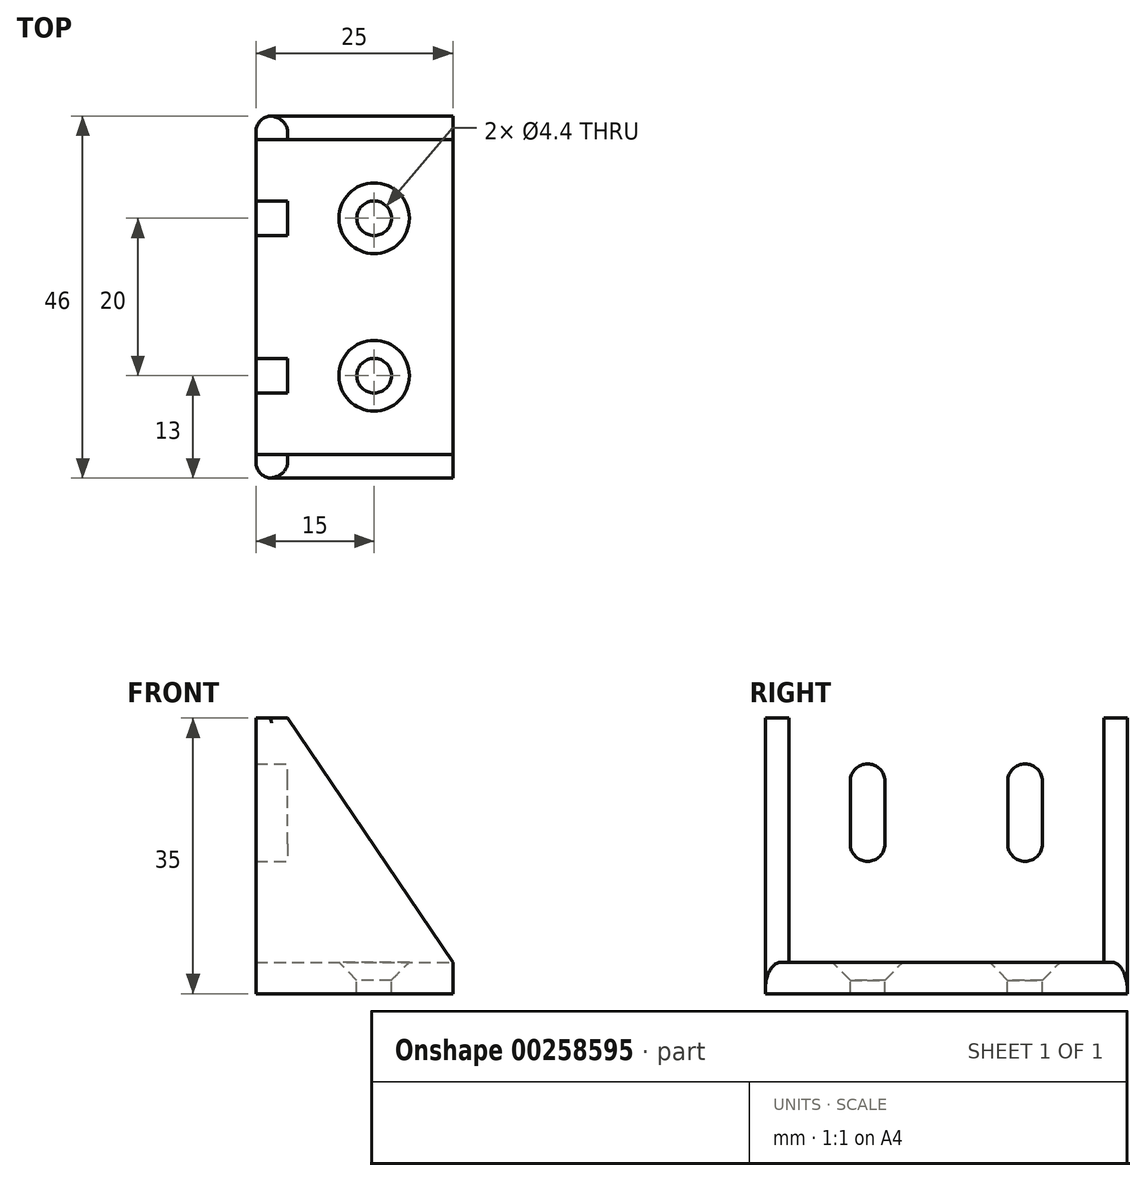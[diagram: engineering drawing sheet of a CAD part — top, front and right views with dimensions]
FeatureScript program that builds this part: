
annotation { "Feature Type Name" : "Feature", "Feature Type Description" : "" }
export const myFeature = defineFeature(function(context is Context, id is Id, definition is map)
    precondition{}
    {
        {
            var Q0;
            Q0=qCreatedBy(makeId("Front.planeOp"),FACE);
            var sketch = newSketch(context, id + "F0", { "sketchPlane" : qUnion([Q0])});
            skLineSegment(sketch, "E0.bottom", {"start": v(-12.5, -17.5) * mm, "end": v(12.5, -17.5) * mm});
            skLineSegment(sketch, "E0.top", {"start": v(-12.5, 17.5) * mm, "end": v(-8.5, 17.5) * mm});
            skLineSegment(sketch, "E0.left", {"start": v(-12.5, -17.5) * mm, "end": v(-12.5, 17.5) * mm});
            skLineSegment(sketch, "E0.right", {"start": v(12.5, -17.5) * mm, "end": v(12.5, -13.5) * mm});
            skPoint(sketch, "E0.middle", {"position": v(0, 0) * mm});
            skLineSegment(sketch, "E1.0", {"start": v(-8.5, -13.5) * mm, "end": v(-8.5, 17.5) * mm});
            skLineSegment(sketch, "E1.1", {"start": v(-8.5, -13.5) * mm, "end": v(12.5, -13.5) * mm});
            skSolve(sketch);
        }
        {
            var Q0;
            Q0 = qSketchRegion(id + "F0", true);
            extrude(context, id + "F1", {"entities" : qUnion([Q0]), "depth" : 40 * mm});
        }
        {
            var Q0;
            Q0=makeQuery(id+"F1.opExtrude","SWEPT_FACE",FACE,{"disambiguationData":[OSD([sQuery(id+"F0.wireOp",EDGE,"E1.0")])]});
            var sketch = newSketch(context, id + "F2", { "sketchPlane" : qUnion([Q0])});
            skPoint(sketch, "E2", {"position": v(-30, 9.5) * mm});
            skPoint(sketch, "E3.1.0.0", {"position": v(-10, 5) * mm});
            skLineSegment(sketch, "E4", {"start": v(-20, 17.5) * mm, "end": v(-20, -13.5) * mm, "construction": true});
            skArc(sketch, "E5", {"start": v(-7.8, 9.5) * mm, "mid": v(-10, 11.7) * mm, "end": v(-12.2, 9.5) * mm});
            skArc(sketch, "E6.MirrorC", {"start": v(-7.8, 1.5) * mm, "mid": v(-10, -0.7) * mm, "end": v(-12.2, 1.5) * mm});
            skArc(sketch, "E7.MirrorC", {"start": v(-32.2, 9.5) * mm, "mid": v(-30, 11.7) * mm, "end": v(-27.8, 9.5) * mm});
            skArc(sketch, "E8.MirrorC", {"start": v(-32.2, 1.5) * mm, "mid": v(-30, -0.7) * mm, "end": v(-27.8, 1.5) * mm});
            skLineSegment(sketch, "E9", {"start": v(-7.8, 1.5) * mm, "end": v(-7.8, 9.5) * mm});
            skLineSegment(sketch, "E10", {"start": v(-12.2, 1.5) * mm, "end": v(-12.2, 9.5) * mm});
            skLineSegment(sketch, "E11.MirrorCS", {"start": v(-27.8, 1.5) * mm, "end": v(-27.8, 9.5) * mm});
            skLineSegment(sketch, "E12.MirrorCS", {"start": v(-32.2, 1.5) * mm, "end": v(-32.2, 9.5) * mm});
            skSolve(sketch);
        }
        {
            var Q0;
            Q0=makeQuery(id+"F2.imprint","IMPRINT",FACE,{"disambiguationData":[TD([[makeQuery(id+"F2.imprint","IMPRINT",EDGE,{"derivedFrom":sQuery(id+"F2.wireOp",EDGE,"E7.MirrorC")}),-1.0]])]});
            var Q1;
            Q1=makeQuery(id+"F2.imprint","IMPRINT",FACE,{"disambiguationData":[TD([[makeQuery(id+"F2.imprint","IMPRINT",EDGE,{"derivedFrom":sQuery(id+"F2.wireOp",EDGE,"E5")}),1.0]])]});
            extrude(context, id + "F3", {"entities" : qUnion([Q0, Q1]), "operationType" : NewBodyOperationType.REMOVE, "endBound" : BoundingType.UP_TO_NEXT, "oppositeDirection" : true, "depth" : 25 * mm});
        }
        {
            var Q0;
            Q0=makeQuery(id+"F1.opExtrude","SWEPT_FACE",FACE,{"disambiguationData":[OSD([sQuery(id+"F0.wireOp",EDGE,"E1.1")])]});
            var sketch = newSketch(context, id + "F4", { "sketchPlane" : qUnion([Q0])});
            skPoint(sketch, "E13", {"position": v(2.5, -30) * mm});
            skLineSegment(sketch, "E14", {"start": v(-8.5, -20) * mm, "end": v(12.5, -20) * mm, "construction": true});
            skPoint(sketch, "E15.MirrorP", {"position": v(2.5, -10) * mm});
            skSolve(sketch);
        }
        {
            var Q0;
            Q0=sQuery(id+"F4.wireOp",VERTEX,"E13");
            var Q1;
            Q1=sQuery(id+"F4.wireOp",VERTEX,"E15.MirrorP");
            var Q2;
            Q2=makeQuery(id+"F1.opExtrude","SWEPT_BODY",BODY,{"disambiguationData":[OSD([sQuery(id+"F0.wireOp",EDGE,"E0.bottom"),sQuery(id+"F0.wireOp",EDGE,"E0.top"),sQuery(id+"F0.wireOp",EDGE,"E0.left"),sQuery(id+"F0.wireOp",EDGE,"E0.right"),sQuery(id+"F0.wireOp",EDGE,"E1.0"),sQuery(id+"F0.wireOp",EDGE,"E1.1")])]});
            hole(context, id + "F5", {"style" : HoleStyle.C_SINK, "endStyle" : HoleEndStyle.THROUGH, "standardTappedOrClearance" : lookupTablePath({ "standard" : "ISO", "fit" : "Normal", "size" : "M4", "type" : "Clearance" }), "standardBlindInLast" : lookupTablePath({ "fit" : "Standard", "standard" : "ISO", "size" : "M4", "type" : "Clearance" }), "holeDiameter" : 4.4 * mm, "cSinkDiameter" : 8.96 * mm, "cSinkAngle" : 90 * degree, "tappedDepth" : 12 * mm, "tapClearance" : 3, "locations" : qUnion([Q0, Q1]), "scope" : qUnion([Q2])});
        }
        {
            var Q0;
            Q0=makeQuery(id+"F1.opExtrude","CAP_FACE",FACE,{"disambiguationData":[OSD([sQuery(id+"F0.wireOp",EDGE,"E0.bottom"),sQuery(id+"F0.wireOp",EDGE,"E0.top"),sQuery(id+"F0.wireOp",EDGE,"E0.left"),sQuery(id+"F0.wireOp",EDGE,"E0.right"),sQuery(id+"F0.wireOp",EDGE,"E1.0"),sQuery(id+"F0.wireOp",EDGE,"E1.1")])],"isStart":false});
            var sketch = newSketch(context, id + "F6", { "sketchPlane" : qUnion([Q0])});
            skLineSegment(sketch, "E16", {"start": v(-8.5, 17.5) * mm, "end": v(12.5, -13.5) * mm});
            skLineSegment(sketch, "E17", {"start": v(12.5, -13.5) * mm, "end": v(12.5, -17.5) * mm});
            skLineSegment(sketch, "E18", {"start": v(12.5, -17.5) * mm, "end": v(-12.5, -17.5) * mm});
            skLineSegment(sketch, "E19", {"start": v(-12.5, -17.5) * mm, "end": v(-12.5, 17.5) * mm});
            skLineSegment(sketch, "E20", {"start": v(-12.5, 17.5) * mm, "end": v(-8.5, 17.5) * mm});
            skSolve(sketch);
        }
        {
            var Q0;
            Q0 = qSketchRegion(id + "F6", true);
            extrude(context, id + "F7", {"entities" : qUnion([Q0]), "operationType" : NewBodyOperationType.ADD, "depth" : 3 * mm});
        }
        {
            var Q0;
            Q0=makeQuery(id+"F1.opExtrude","CAP_FACE",FACE,{"disambiguationData":[OSD([sQuery(id+"F0.wireOp",EDGE,"E0.bottom"),sQuery(id+"F0.wireOp",EDGE,"E0.top"),sQuery(id+"F0.wireOp",EDGE,"E0.left"),sQuery(id+"F0.wireOp",EDGE,"E0.right"),sQuery(id+"F0.wireOp",EDGE,"E1.0"),sQuery(id+"F0.wireOp",EDGE,"E1.1")])],"isStart":true});
            cPlane(context, id + "F8", {"entities" : qUnion([Q0]), "cplaneType" : CPlaneType.OFFSET, "offset" : 20 * mm, "oppositeDirection" : true, "width" : 150 * mm, "height" : 150 * mm});
        }
        {
            var Q0;
            Q0=makeQuery(id+"F1.opExtrude","SWEPT_BODY",BODY,{"disambiguationData":[OSD([sQuery(id+"F0.wireOp",EDGE,"E0.bottom"),sQuery(id+"F0.wireOp",EDGE,"E0.top"),sQuery(id+"F0.wireOp",EDGE,"E0.left"),sQuery(id+"F0.wireOp",EDGE,"E0.right"),sQuery(id+"F0.wireOp",EDGE,"E1.0"),sQuery(id+"F0.wireOp",EDGE,"E1.1")])]});
            var Q1;
            Q1=qCreatedBy(id+"F8.planeOp",FACE);
            mirror(context, id + "F9", {"operationType" : NewBodyOperationType.ADD, "entities" : qUnion([Q0]), "mirrorPlane" : qUnion([Q1])});
        }
        {
            var Q0;
            Q0=makeQuery(id+"F1.opExtrude","CAP_EDGE",EDGE,{"disambiguationData":[OSD([sQuery(id+"F0.wireOp",EDGE,"E1.0")])],"isStart":false});
            var Q1;
            Q1=makeQuery(id+"F1.opExtrude","CAP_EDGE",EDGE,{"disambiguationData":[OSD([sQuery(id+"F0.wireOp",EDGE,"E1.1")])],"isStart":false});
            var Q2;
            Q2=makeQuery(id+"F1.opExtrude","SWEPT_EDGE",EDGE,{"disambiguationData":[OSD([sQuery(id+"F0.wireOp",EDGE,"E1.0"),sQuery(id+"F0.wireOp",EDGE,"E1.1")])]});
            var Q3;
            {var subQ0=sQuery(id+"F0.wireOp",EDGE,"E1.1");Q3=makeQuery(id+"F9.boolean.opBoolean","MERGE",EDGE,{"derivedFrom":[makeQuery(id+"F1.opExtrude","CAP_EDGE",EDGE,{"disambiguationData":[OSD([subQ0])],"isStart":true}),makeQuery(id+"F9.opPattern","COPY",EDGE,{"derivedFrom":makeQuery(id+"F1.opExtrude","CAP_EDGE",EDGE,{"disambiguationData":[OSD([subQ0])],"isStart":false}),"instanceName":"1"})]});}
            var Q4;
            {var subQ0=sQuery(id+"F0.wireOp",EDGE,"E1.0");Q4=makeQuery(id+"F9.boolean.opBoolean","MERGE",EDGE,{"derivedFrom":[makeQuery(id+"F1.opExtrude","CAP_EDGE",EDGE,{"disambiguationData":[OSD([subQ0])],"isStart":true}),makeQuery(id+"F9.opPattern","COPY",EDGE,{"derivedFrom":makeQuery(id+"F1.opExtrude","CAP_EDGE",EDGE,{"disambiguationData":[OSD([subQ0])],"isStart":false}),"instanceName":"1"})]});}
            var Q5;
            Q5=makeQuery(id+"F9.opPattern","COPY",EDGE,{"derivedFrom":makeQuery(id+"F7.opExtrude","CAP_EDGE",EDGE,{"disambiguationData":[OSD([sQuery(id+"F6.wireOp",EDGE,"E16")])],"isStart":false}),"instanceName":"1"});
            var Q6;
            Q6=makeQuery(id+"F7.opExtrude","CAP_EDGE",EDGE,{"disambiguationData":[OSD([sQuery(id+"F6.wireOp",EDGE,"E16")])],"isStart":false});
            fillet(context, id + "F10", {"entities" : qUnion([Q0, Q1, Q2, Q3, Q4, Q5, Q6]), "radius" : 2 * mm, "tangentPropagation" : true, "allowEdgeOverflow" : false});
        }
        {
            var Q0;
            Q0=makeQuery(id+"F9.opPattern","COPY",EDGE,{"derivedFrom":makeQuery(id+"F7.opExtrude","CAP_EDGE",EDGE,{"disambiguationData":[OSD([sQuery(id+"F6.wireOp",EDGE,"E19")])],"isStart":false}),"instanceName":"1"});
            var Q1;
            Q1=makeQuery(id+"F7.opExtrude","CAP_EDGE",EDGE,{"disambiguationData":[OSD([sQuery(id+"F6.wireOp",EDGE,"E19")])],"isStart":false});
            fillet(context, id + "F11", {"entities" : qUnion([Q0, Q1]), "radius" : 2 * mm, "tangentPropagation" : true, "allowEdgeOverflow" : false});
        }
    });
